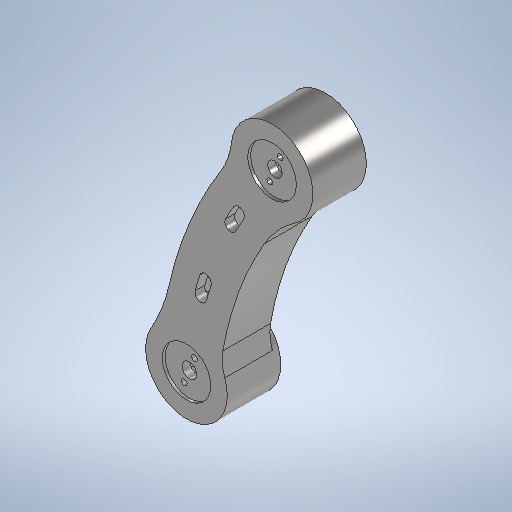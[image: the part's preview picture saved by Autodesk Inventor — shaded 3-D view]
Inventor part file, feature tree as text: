
AUTODESK INVENTOR PART (.ipt)
format: ipt  version: 2025.1 (Build 291241020, 241B)  size: 503,808 bytes
history: native  units: mm
features: sketch x8, extrude x7, projected_geometry x3, revolve x2, shell x1, chamfer x1, plane x1
ambient origin geometry x8: Origin, YZ Plane, XZ Plane, XY Plane, X Axis, Y Axis, Z Axis, Center Point
bodies: Solid1 (feature_tree)
feature tree (23):
  sketch  "Sketch2"  dims[d26=42.0mm d51=27.5mm d52=0.0mm d53=25.0mm d54=1.5mm d55=0.0mm]
  extrude  "Extrusion6"  Depth=27.5mm TaperAngle=0.0deg
  shell  "Shell1"  Thickness=25.0mm
  chamfer  "Chamfer1"  Distance=1.5mm
  extrude  "Extrusion9"  Depth=7.5mm
  extrude  "Extrusion1"  Depth=3.759439mm
  extrude  "Extrusion2"  Depth=32.0mm
  extrude  "Extrusion3"  Depth=32.0mm
  extrude  "Extrusion4"  TaperAngle=90.0deg  [1 undecoded]
  revolve  "Revolution1"  [1 undecoded]
  plane  "Work Plane1"
  revolve  "Revolution2"  [1 undecoded]
  extrude  "Extrusion5"  Depth=176.5mm
  sketch  "Sketch3"  dims[d56=7.5mm d57=14.5mm]
  sketch  "Sketch4"  dims[d58=3.0mm d61=3.759439mm]
  sketch  "Sketch5"  dims[d62=1.5mm d63=0.0mm d64=32.0mm]
  sketch  "Sketch6"  dims[d65=1.0mm d66=0.0mm d67=32.0mm]
  sketch  "Sketch7"  dims[d70=13.0mm d71=90.0deg]
  projected_geometry  "Projected Loop1"
  projected_geometry  "Projected Loop2"
  sketch  "Sketch8"  dims[d73=22.0mm d74=0.0mm d81=18.749mm]
  projected_geometry  "Projected Loop3"
  sketch  "Sketch13"  dims[d82=77.251mm d83=40.142mm d86=176.5mm d88=94.306mm d89=22.694mm d92=53.037mm d93=87.399mm d95=10.432mm d96=34.233mm d97=8.904mm d98=98.561mm d99=17.748mm d100=114.146mm d101=206.278mm d102=7.18mm d103=111.617mm d104=44.064mm d106=3.759439mm d107=44.064mm d108=32.0mm d109=13.0mm d110=90.0deg d112=13.75mm d113=0.0mm d116=10.75mm d117=0.0mm d118=5.0mm d130=5.0mm d131=2.0mm d132=45.0deg d136=6.0mm d141=1.308997mm d142=0.0mm d143=0.0mm d144=0.436332mm d145=0.436332mm d146=119.999962mm]
note: 3 required parameter values undecoded (feature->parameter linkage not recoverable at this tier; creation-order binding heuristic only, values carry confidence <= 0.55)